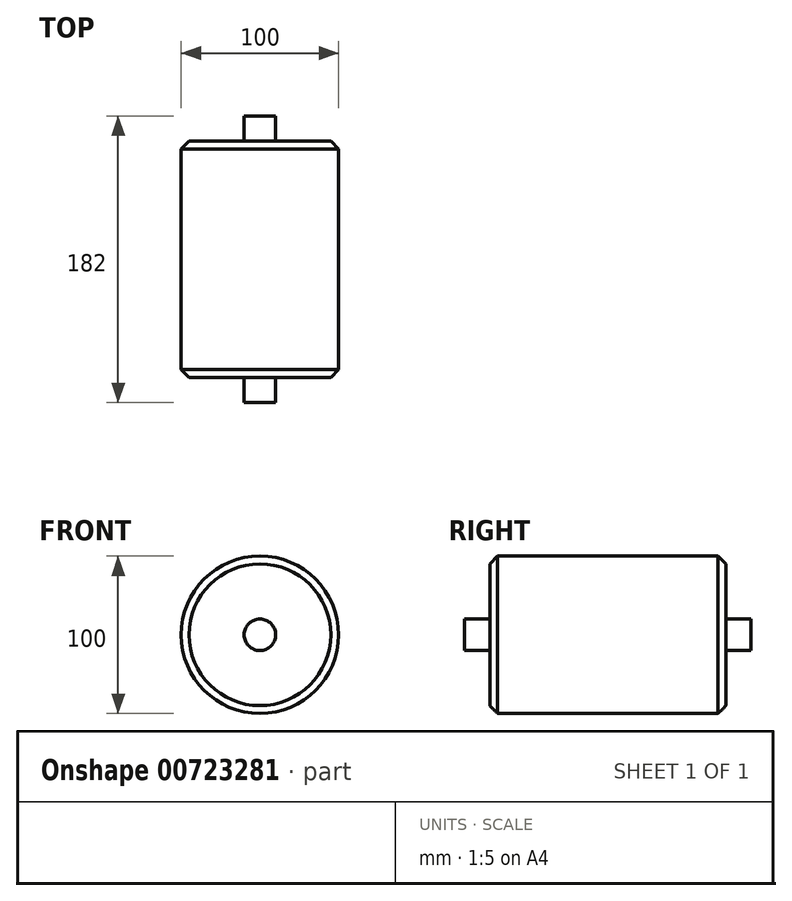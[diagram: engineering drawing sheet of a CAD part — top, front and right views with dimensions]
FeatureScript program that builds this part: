
annotation { "Feature Type Name" : "Feature", "Feature Type Description" : "" }
export const myFeature = defineFeature(function(context is Context, id is Id, definition is map)
    precondition{}
    {
        {
            var Q0;
            Q0=qCreatedBy(makeId("Front.planeOp"),FACE);
            var sketch = newSketch(context, id + "F0", { "sketchPlane" : qUnion([Q0])});
            skCircle(sketch, "E0", {"center": v(0, 0) * mm, "radius": 50 * mm});
            skSolve(sketch);
        }
        {
            var Q0;
            Q0 = qSketchRegion(id + "F0", true);
            extrude(context, id + "F1", {"entities" : qUnion([Q0]), "depth" : 150 * mm, "offsetDistance" : 25.4 * mm});
        }
        {
            var Q0;
            Q0=makeQuery(id+"F1.opExtrude","SWEPT_FACE",FACE,{"disambiguationData":[OSD([sQuery(id+"F0.wireOp",EDGE,"E0")])]});
            chamfer(context, id + "F2", {"entities" : qUnion([Q0]), "chamferType" : ChamferType.TWO_OFFSETS, "width1" : 5 * mm, "oppositeDirection" : false, "width2" : 5 * mm, "tangentPropagation" : true});
        }
        {
            var Q0;
            Q0=makeQuery(id+"F1.opExtrude","CAP_FACE",FACE,{"disambiguationData":[OSD([sQuery(id+"F0.wireOp",EDGE,"E0")])],"isStart":true});
            var sketch = newSketch(context, id + "F3", { "sketchPlane" : qUnion([Q0])});
            skCircle(sketch, "E1", {"center": v(0, 0) * mm, "radius": 10 * mm});
            skSolve(sketch);
        }
        {
            var Q0;
            Q0 = qSketchRegion(id + "F3", true);
            extrude(context, id + "F4", {"entities" : qUnion([Q0]), "operationType" : NewBodyOperationType.ADD, "depth" : 16 * mm, "offsetDistance" : 25.4 * mm});
        }
        {
            var Q0;
            Q0=makeQuery(id+"F1.opExtrude","CAP_FACE",FACE,{"disambiguationData":[OSD([sQuery(id+"F0.wireOp",EDGE,"E0")])],"isStart":false});
            var sketch = newSketch(context, id + "F5", { "sketchPlane" : qUnion([Q0])});
            skCircle(sketch, "E2", {"center": v(0, 0) * mm, "radius": 10 * mm});
            skSolve(sketch);
        }
        {
            var Q0;
            Q0 = qSketchRegion(id + "F5", true);
            extrude(context, id + "F6", {"entities" : qUnion([Q0]), "operationType" : NewBodyOperationType.ADD, "depth" : 16 * mm, "offsetDistance" : 25.4 * mm});
        }
        {
            var Q0;
            Q0=makeQuery(id+"F6.opExtrude","CAP_FACE",FACE,{"disambiguationData":[OSD([sQuery(id+"F5.wireOp",EDGE,"E2")])],"isStart":false});
            extrude(context, id + "F7", {"entities" : qUnion([Q0]), "oppositeDirection" : true, "depth" : 16 * mm, "offsetDistance" : 25.4 * mm});
        }
    });
